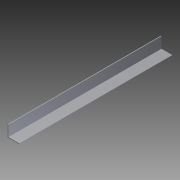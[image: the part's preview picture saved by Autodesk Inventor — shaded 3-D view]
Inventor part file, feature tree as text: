
AUTODESK INVENTOR PART (.ipt)
format: ipt  version: 2012 (Build 160160000, 160)  size: 72,192 bytes
history: native  units: in
note: dims shown in document units (in); Inventor stores cm internally (conversion verified against a paired STEP export)
features: extrude x1, sketch x1
ambient origin geometry x8: Origin, YZ Plane, XZ Plane, XY Plane, X Axis, Y Axis, Z Axis, Center Point
bodies: Solid1 (feature_tree)
feature tree (2):
  extrude  "Extrusion1"  Depth=0.0625in
  sketch  "Sketch1"  dims[d0=0.0625in d1=0.0625in d2=1.0in d3=1.0in d4=13.1875in d5=0.0in]
